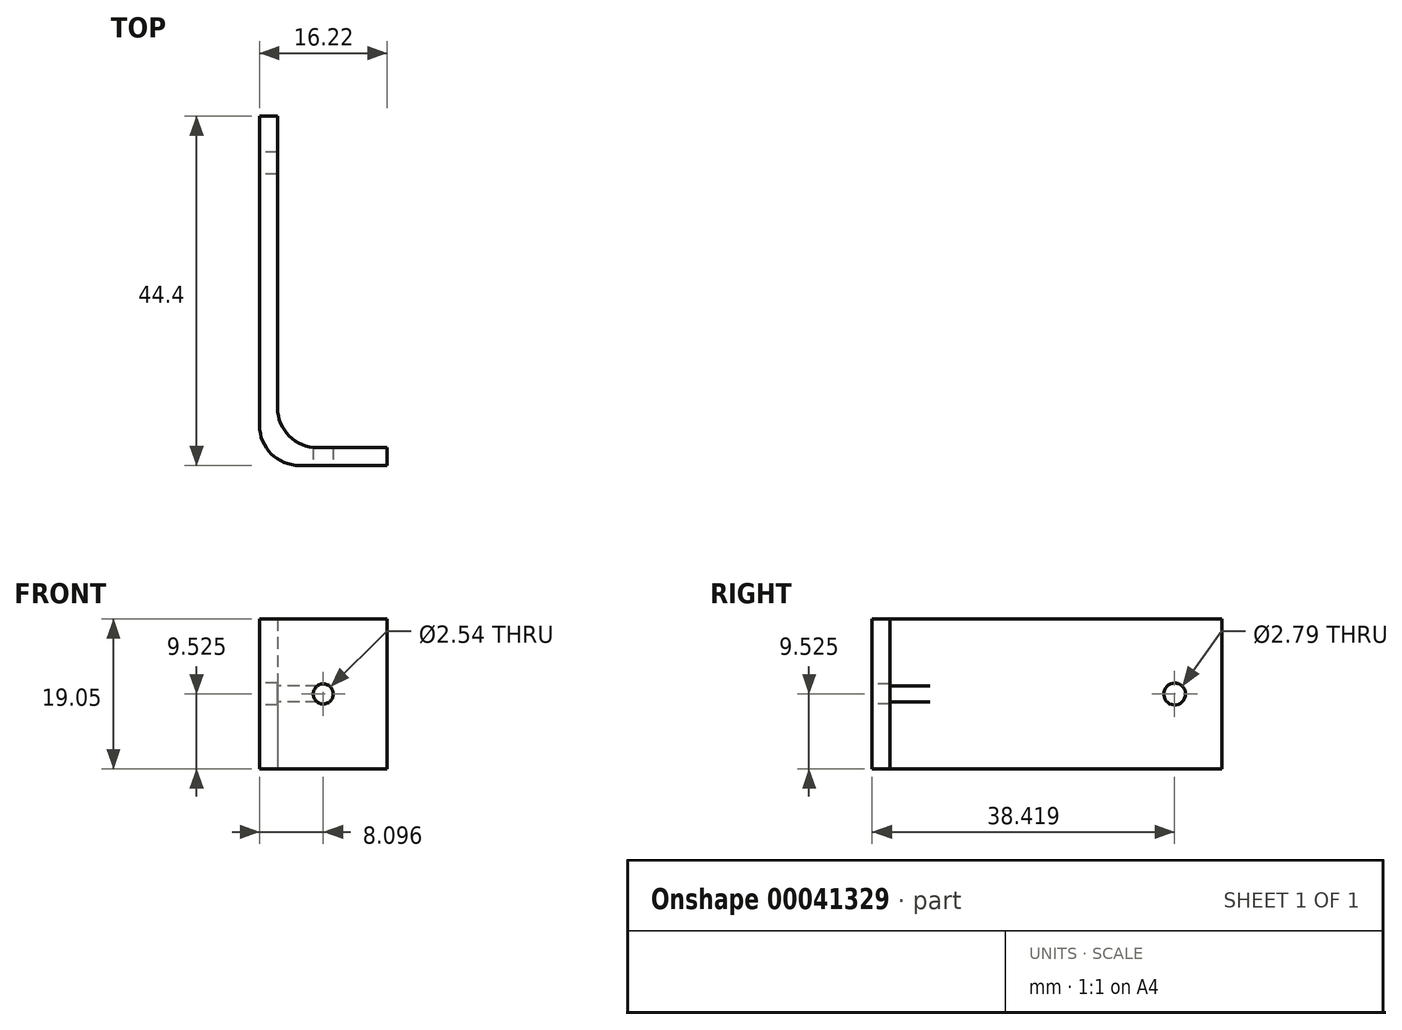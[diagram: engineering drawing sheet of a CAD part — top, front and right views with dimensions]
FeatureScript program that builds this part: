
annotation { "Feature Type Name" : "Feature", "Feature Type Description" : "" }
export const myFeature = defineFeature(function(context is Context, id is Id, definition is map)
    precondition{}
    {
        {
            var Q0;
            Q0=qCreatedBy(makeId("Top.planeOp"),FACE);
            var sketch = newSketch(context, id + "F0", { "sketchPlane" : qUnion([Q0])});
            skLineSegment(sketch, "E0.bottom", {"start": v(0, 22.6) * mm, "end": v(2.28, 22.6) * mm});
            skLineSegment(sketch, "E0.top", {"start": v(0, -10.56) * mm, "end": v(2.28, -10.56) * mm});
            skLineSegment(sketch, "E0.left", {"start": v(0, 22.6) * mm, "end": v(0, -10.56) * mm});
            skLineSegment(sketch, "E0.right", {"start": v(2.28, 22.6) * mm, "end": v(2.28, -10.56) * mm});
            skLineSegment(sketch, "E1.bottom", {"start": v(2.28, -10.56) * mm, "end": v(16.22, -10.56) * mm});
            skLineSegment(sketch, "E1.top", {"start": v(2.28, -8.3) * mm, "end": v(16.22, -8.3) * mm});
            skLineSegment(sketch, "E1.left", {"start": v(2.28, -10.56) * mm, "end": v(2.28, -8.3) * mm});
            skLineSegment(sketch, "E1.right", {"start": v(16.22, -10.56) * mm, "end": v(16.22, -8.3) * mm});
            skLineSegment(sketch, "E2", {"start": v(0, 22.6) * mm, "end": v(0, 33.84) * mm});
            skLineSegment(sketch, "E3", {"start": v(0, 33.84) * mm, "end": v(2.27, 33.84) * mm});
            skLineSegment(sketch, "E4", {"start": v(2.27, 33.84) * mm, "end": v(2.28, 22.6) * mm});
            skSolve(sketch);
        }
        {
            var Q0;
            Q0 = qSketchRegion(id + "F0", true);
            extrude(context, id + "F1", {"entities" : qUnion([Q0]), "depth" : 19.05 * mm});
        }
        {
            var Q0;
            Q0=makeQuery(id+"F1.opExtrude","SWEPT_FACE",FACE,{"disambiguationData":[OSD([sQuery(id+"F0.wireOp",EDGE,"E0.left"),sQuery(id+"F0.wireOp",EDGE,"E2")])]});
            var sketch = newSketch(context, id + "F2", { "sketchPlane" : qUnion([Q0])});
            skCircle(sketch, "E5", {"center": v(-27.86, 9.53) * mm, "radius": 1.4 * mm});
            skPoint(sketch, "E5.centerSnap0", {"position": v(-33.84, 9.53) * mm});
            skSolve(sketch);
        }
        {
            var Q0;
            Q0 = qSketchRegion(id + "F2", true);
            extrude(context, id + "F3", {"entities" : qUnion([Q0]), "operationType" : NewBodyOperationType.REMOVE, "endBound" : BoundingType.UP_TO_NEXT, "oppositeDirection" : true, "depth" : 25.4 * mm});
        }
        {
            var Q0;
            Q0=makeQuery(id+"F1.opExtrude","SWEPT_FACE",FACE,{"disambiguationData":[OSD([sQuery(id+"F0.wireOp",EDGE,"E0.top"),sQuery(id+"F0.wireOp",EDGE,"E1.bottom")])]});
            var sketch = newSketch(context, id + "F4", { "sketchPlane" : qUnion([Q0])});
            skCircle(sketch, "E6", {"center": v(8.1, 9.53) * mm, "radius": 1.27 * mm});
            skPoint(sketch, "E6.centerSnap0", {"position": v(16.22, 9.53) * mm});
            skSolve(sketch);
        }
        {
            var Q0;
            Q0 = qSketchRegion(id + "F4", true);
            extrude(context, id + "F5", {"entities" : qUnion([Q0]), "operationType" : NewBodyOperationType.REMOVE, "endBound" : BoundingType.UP_TO_NEXT, "oppositeDirection" : true, "depth" : 25.4 * mm});
        }
        {
            var Q0;
            Q0=makeQuery(id+"F1.opExtrude","SWEPT_EDGE",EDGE,{"disambiguationData":[OSD([sQuery(id+"F0.wireOp",EDGE,"E0.bottom"),sQuery(id+"F0.wireOp",EDGE,"E0.left"),sQuery(id+"F0.wireOp",EDGE,"6bb3e5f2-a65a-4e7b-b264-85912e62ca72")])]});
            var Q1;
            Q1=makeQuery(id+"F1.opExtrude","SWEPT_EDGE",EDGE,{"disambiguationData":[OSD([sQuery(id+"F0.wireOp",EDGE,"E0.right"),sQuery(id+"F0.wireOp",EDGE,"b33e8b98-3b22-4776-ae92-11d1b4bd1c30")])]});
            fillet(context, id + "F6", {"entities" : qUnion([Q0, Q1]), "radius" : 5.08 * mm, "tangentPropagation" : true, "allowEdgeOverflow" : false});
        }
    });
